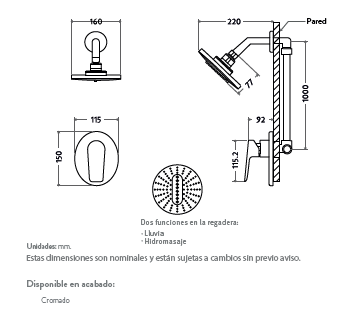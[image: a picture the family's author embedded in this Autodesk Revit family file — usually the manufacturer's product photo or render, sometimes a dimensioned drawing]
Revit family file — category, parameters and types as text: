
# Revit family: PM4035551_Mezclador Monocontrol Palma SD
name_source: partatom
category: Plumbing Fixtures
units: mm (PartAtom-declared; Revit-internal decimal feet)

## family parameters
Always vertical = Yes
Cut with Voids When Loaded = No
Host = Wall
OmniClass Number = 23.31.15.11
OmniClass Title = Bath Shower Units
Part Type = Normal
Room Calculation Point = No
Round Connector Dimension = Use Diameter
Shared = No

## types (1)
- PM4035551_Mezclador monocontrol palma
    ALTO = 2000 mm  [stored 6.56168 ft]
    ALTO_MEZCLADOR = 1200 mm
    Alto = 860 mm
    Altura ducha = 2000 mm  [stored 6.56168 ft]
    Altura mezclador = 1200 mm
    Ancho = 179 mm  [stored 0.58727 ft]
    Capacidad de flujo máximo a 80 psi = 9.5 L/min.
    Creado por = IDD
    Description = Grifería de Duchas con ahorro de agua.
• Acabado superior, mayor espesor en el cromado que lo hace
más brillante y resistente a la corrosión.
• Brazo con mayor longitud que permite mayor alcance dando
confort en el uso.
• Fácil limpieza: diseño que evita la acumulación de impurezas.
    Fabricante = Corona
    Fecha de creación = 10/08/2020
    Garantía = 30 años
    Garantía Acabados = 2 años
    Material = Corona_Plastico_Cromado
    Peso neto = 1.070 gr. - 2.359 lb.
    Presion maxima = 125 psi (862 Kpa).
    Presion minima = 20 psi (138 Kpa).
    Temperatura de uso = 5ºC a 71ºC.
    Vida útil o desgaste (regadera) = 10.000 ciclos.
    Vida útil o desgaste (unidad) = 250.000 ciclos.

note: [stored X ft] marks values corroborated as IEEE doubles in the binary element streams (Revit-internal decimal feet)

## geometry (parser evidence)
native form markers: Blend x3, Extrusion x1, Sweep x7
no freeform markers — native parametric forms only
